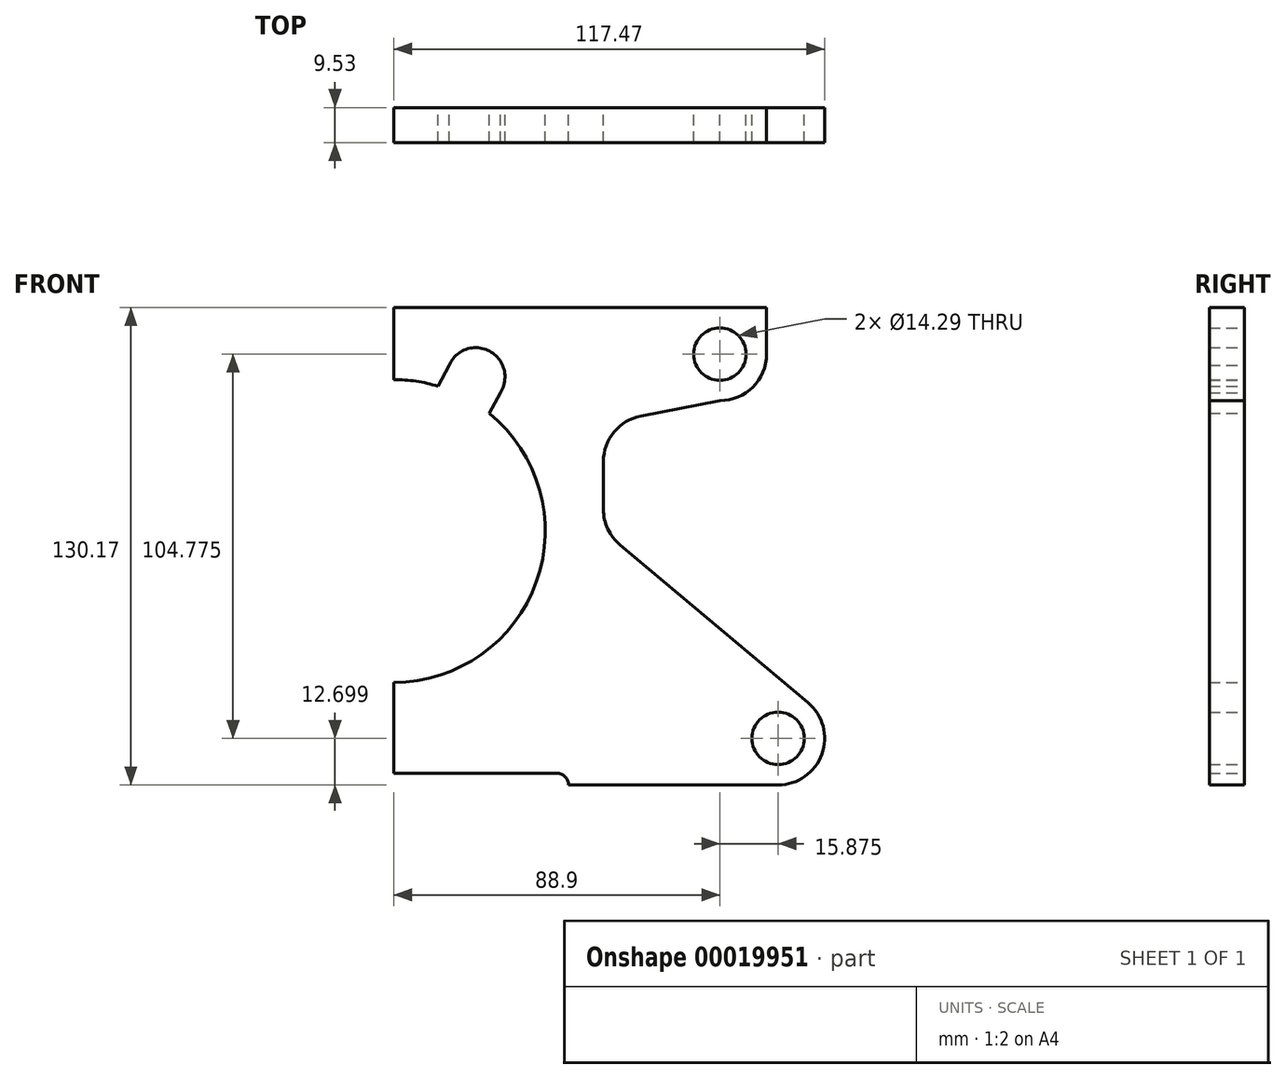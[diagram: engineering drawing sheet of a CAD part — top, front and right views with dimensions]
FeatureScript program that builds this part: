
annotation { "Feature Type Name" : "Feature", "Feature Type Description" : "" }
export const myFeature = defineFeature(function(context is Context, id is Id, definition is map)
    precondition{}
    {
        {
            var Q0;
            Q0=qCreatedBy(makeId("Front.planeOp"),FACE);
            var sketch = newSketch(context, id + "F0", { "sketchPlane" : qUnion([Q0])});
            skLineSegment(sketch, "E0.bottom", {"start": v(0, 60.93) * mm, "end": v(101.6, 60.93) * mm});
            skLineSegment(sketch, "E0.top", {"start": v(47.63, -69.24) * mm, "end": v(101.6, -69.24) * mm});
            skLineSegment(sketch, "E0.left", {"start": v(0, 60.93) * mm, "end": v(0, -66.07) * mm});
            skLineSegment(sketch, "E0.right", {"start": v(101.6, 60.93) * mm, "end": v(101.6, 48.23) * mm});
            skLineSegment(sketch, "E1", {"start": v(101.6, 60.93) * mm, "end": v(88.9, 60.93) * mm});
            skCircle(sketch, "E2", {"center": v(88.9, 48.23) * mm, "radius": 7.14 * mm});
            skArc(sketch, "E3", {"start": v(88.9, 35.53) * mm, "mid": v(97.88, 39.25) * mm, "end": v(101.6, 48.23) * mm});
            skLineSegment(sketch, "E4", {"start": v(88.9, 35.53) * mm, "end": v(67.43, 31.36) * mm});
            skLineSegment(sketch, "E5", {"start": v(57.15, 18.9) * mm, "end": v(57.15, 5.92) * mm});
            skPoint(sketch, "E6.newPointB", {"position": v(57.15, 50.8) * mm});
            skArc(sketch, "E6.filletArc", {"start": v(67.43, 31.36) * mm, "mid": v(60.05, 26.97) * mm, "end": v(57.15, 18.9) * mm});
            skLineSegment(sketch, "E7.top", {"start": v(0, -66.07) * mm, "end": v(44.45, -66.07) * mm});
            skLineSegment(sketch, "E7.right", {"start": v(47.63, -69.24) * mm, "end": v(47.63, -69.24) * mm});
            skPoint(sketch, "E8.visualSharp", {"position": v(47.63, -66.07) * mm});
            skArc(sketch, "E8.filletArc", {"start": v(47.63, -69.24) * mm, "mid": v(46.7, -67) * mm, "end": v(44.45, -66.07) * mm});
            skLineSegment(sketch, "E9", {"start": v(101.6, -69.24) * mm, "end": v(104.78, -69.24) * mm});
            skCircle(sketch, "E10", {"center": v(104.78, -56.54) * mm, "radius": 7.14 * mm});
            skArc(sketch, "E11", {"start": v(104.78, -69.24) * mm, "mid": v(116.7, -60.88) * mm, "end": v(112.94, -46.81) * mm});
            skLineSegment(sketch, "E12", {"start": v(61.69, -3.8) * mm, "end": v(112.94, -46.81) * mm});
            skPoint(sketch, "E13.visualSharp", {"position": v(57.15, 0) * mm});
            skArc(sketch, "E13.filletArc", {"start": v(57.15, 5.92) * mm, "mid": v(58.34, 0.55) * mm, "end": v(61.69, -3.8) * mm});
            skPoint(sketch, "E14.end.orphan", {"position": v(139.67, -69.24) * mm});
            skArc(sketch, "E15", {"start": v(0, -41.28) * mm, "mid": v(38.9, -13.8) * mm, "end": v(26, 32.05) * mm});
            skArc(sketch, "E16.MirrorCS", {"start": v(-47.63, -69.24) * mm, "mid": v(-46.7, -67) * mm, "end": v(-44.45, -66.07) * mm});
            skLineSegment(sketch, "E17.MirrorCS", {"start": v(-101.6, -69.24) * mm, "end": v(-104.78, -69.24) * mm});
            skArc(sketch, "E18.MirrorCS", {"start": v(-57.15, 5.92) * mm, "mid": v(-58.34, 0.55) * mm, "end": v(-61.69, -3.8) * mm});
            skLineSegment(sketch, "E19.MirrorCS", {"start": v(-101.6, 60.93) * mm, "end": v(-88.9, 60.93) * mm});
            skArc(sketch, "E20.MirrorCS", {"start": v(0, -41.28) * mm, "mid": v(-41.28, 0) * mm, "end": v(0, 41.28) * mm});
            skArc(sketch, "E21.MirrorCS", {"start": v(-67.43, 31.36) * mm, "mid": v(-60.05, 26.97) * mm, "end": v(-57.15, 18.9) * mm});
            skLineSegment(sketch, "E22.MirrorCS", {"start": v(0, -66.07) * mm, "end": v(-44.45, -66.07) * mm});
            skLineSegment(sketch, "E23.MirrorCS", {"start": v(-88.9, 35.53) * mm, "end": v(-67.43, 31.36) * mm});
            skLineSegment(sketch, "E24.MirrorCS", {"start": v(0, 60.93) * mm, "end": v(-101.6, 60.93) * mm});
            skLineSegment(sketch, "E25.MirrorCS", {"start": v(-61.69, -3.8) * mm, "end": v(-112.94, -46.81) * mm});
            skLineSegment(sketch, "E26.MirrorCS", {"start": v(-57.15, 18.9) * mm, "end": v(-57.15, 5.92) * mm});
            skPoint(sketch, "E27.MirrorP", {"position": v(-139.67, -69.24) * mm});
            skLineSegment(sketch, "E28.MirrorCS", {"start": v(-47.63, -69.24) * mm, "end": v(-101.6, -69.24) * mm});
            skLineSegment(sketch, "E29.MirrorCS", {"start": v(-101.6, 60.93) * mm, "end": v(-101.6, 48.23) * mm});
            skPoint(sketch, "E30.MirrorP", {"position": v(-47.63, -66.07) * mm});
            skArc(sketch, "E31.MirrorCS", {"start": v(-88.9, 35.53) * mm, "mid": v(-97.88, 39.25) * mm, "end": v(-101.6, 48.23) * mm});
            skCircle(sketch, "E32.MirrorC", {"center": v(-88.9, 48.23) * mm, "radius": 7.14 * mm});
            skCircle(sketch, "E33.MirrorC", {"center": v(-104.78, -56.54) * mm, "radius": 7.14 * mm});
            skPoint(sketch, "E34.MirrorP", {"position": v(-57.15, 50.8) * mm});
            skArc(sketch, "E35.MirrorCS", {"start": v(-104.78, -69.24) * mm, "mid": v(-116.7, -60.88) * mm, "end": v(-112.94, -46.81) * mm});
            skPoint(sketch, "E36.MirrorP", {"position": v(-57.15, 0) * mm});
            skCircle(sketch, "E37", {"center": v(-58.74, -53.37) * mm, "radius": 9.53 * mm});
            skArc(sketch, "E38", {"start": v(29.03, 37.75) * mm, "mid": v(26.09, 49.06) * mm, "end": v(15.06, 45.18) * mm});
            skLineSegment(sketch, "E39", {"start": v(15.06, 45.18) * mm, "end": v(12.03, 39.48) * mm});
            skLineSegment(sketch, "E40", {"start": v(29.03, 37.75) * mm, "end": v(26, 32.05) * mm});
            skArc(sketch, "E41.trimOffspring", {"start": v(12.03, 39.48) * mm, "mid": v(6.08, 40.82) * mm, "end": v(0, 41.28) * mm});
            skSolve(sketch);
        }
        {
            var Q0;
            Q0=makeQuery(id+"F0.imprint","IMPRINT",FACE,{"disambiguationData":[TD([[makeQuery(id+"F0.imprint","IMPRINT",EDGE,{"derivedFrom":sQuery(id+"F0.wireOp",EDGE,"E16.MirrorCS")}),1.0]])]});
            var Q1;
            {var subQ5=sQuery(id+"F0.wireOp",EDGE,"E0.bottom");Q1=makeQuery(id+"F0.imprint","IMPRINT",FACE,{"disambiguationData":[TD([[makeQuery(id+"F0.imprint","IMPRINT",EDGE,{"derivedFrom":subQ5}),-1.0]])]});}
            extrude(context, id + "F1", {"entities" : qUnion([Q0, Q1]), "depth" : 9.52 * mm});
        }
    });
